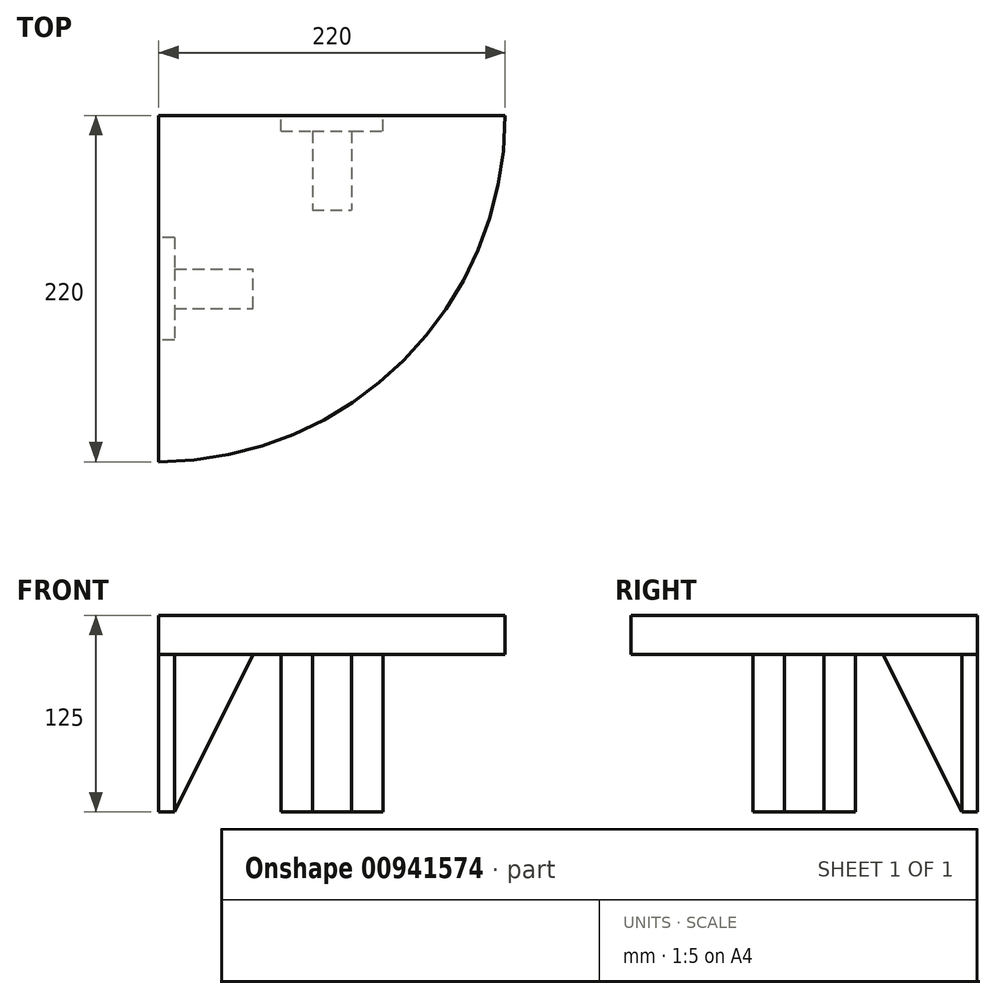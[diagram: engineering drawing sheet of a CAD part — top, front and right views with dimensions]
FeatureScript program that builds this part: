
annotation { "Feature Type Name" : "Feature", "Feature Type Description" : "" }
export const myFeature = defineFeature(function(context is Context, id is Id, definition is map)
    precondition{}
    {
        {
            var Q0;
            Q0=qCreatedBy(makeId("Top.planeOp"),FACE);
            var sketch = newSketch(context, id + "F0", { "sketchPlane" : qUnion([Q0])});
            skLineSegment(sketch, "E0", {"start": v(0, 0) * mm, "end": v(0, -220) * mm});
            skLineSegment(sketch, "E1", {"start": v(0, 0) * mm, "end": v(220, 0) * mm});
            skCircle(sketch, "E2", {"center": v(0, 0) * mm, "radius": 220 * mm});
            skSolve(sketch);
        }
        {
            var Q0;
            {var subQ0=sQuery(id+"F0.wireOp",EDGE,"E0");Q0=makeQuery(id+"F0.imprint","IMPRINT",FACE,{"disambiguationData":[TD([[makeQuery(id+"F0.imprint","IMPRINT",EDGE,{"derivedFrom":subQ0}),1.0]])]});}
            extrude(context, id + "F1", {"entities" : qUnion([Q0]), "oppositeDirection" : true, "depth" : 25 * mm, "offsetDistance" : 25 * mm});
        }
        {
            var Q0;
            Q0=makeQuery(id+"F1.opExtrude","SWEPT_FACE",FACE,{"disambiguationData":[OSD([sQuery(id+"F0.wireOp",EDGE,"E1")])]});
            var sketch = newSketch(context, id + "F2", { "sketchPlane" : qUnion([Q0])});
            skLineSegment(sketch, "E3", {"start": v(-110, -25) * mm, "end": v(-77.5, -25) * mm, "construction": true});
            skLineSegment(sketch, "E4.bottom", {"start": v(-77.5, -25) * mm, "end": v(-142.5, -25) * mm});
            skLineSegment(sketch, "E4.top", {"start": v(-77.5, -125) * mm, "end": v(-142.5, -125) * mm});
            skLineSegment(sketch, "E4.left", {"start": v(-77.5, -25) * mm, "end": v(-77.5, -125) * mm});
            skLineSegment(sketch, "E4.right", {"start": v(-142.5, -25) * mm, "end": v(-142.5, -125) * mm});
            skPoint(sketch, "E5", {"position": v(-122.5, -25) * mm});
            skLineSegment(sketch, "E6.bottom", {"start": v(-122.5, -25) * mm, "end": v(-97.5, -25) * mm});
            skLineSegment(sketch, "E6.top", {"start": v(-122.5, -125) * mm, "end": v(-97.5, -125) * mm});
            skLineSegment(sketch, "E6.left", {"start": v(-122.5, -25) * mm, "end": v(-122.5, -125) * mm});
            skLineSegment(sketch, "E6.right", {"start": v(-97.5, -25) * mm, "end": v(-97.5, -125) * mm});
            skSolve(sketch);
        }
        {
            var Q0;
            {var subQ0=sQuery(id+"F2.wireOp",EDGE,"E6.left");Q0=makeQuery(id+"F2.imprint","IMPRINT",FACE,{"disambiguationData":[TD([[makeQuery(id+"F2.imprint","IMPRINT",EDGE,{"derivedFrom":subQ0}),1.0]])]});}
            var Q1;
            {var subQ0=sQuery(id+"F2.wireOp",EDGE,"E4.right");Q1=makeQuery(id+"F2.imprint","IMPRINT",FACE,{"disambiguationData":[TD([[makeQuery(id+"F2.imprint","IMPRINT",EDGE,{"derivedFrom":subQ0}),1.0]])]});}
            var Q2;
            {var subQ0=sQuery(id+"F2.wireOp",EDGE,"E4.left");Q2=makeQuery(id+"F2.imprint","IMPRINT",FACE,{"disambiguationData":[TD([[makeQuery(id+"F2.imprint","IMPRINT",EDGE,{"derivedFrom":subQ0}),-1.0]])]});}
            extrude(context, id + "F3", {"entities" : qUnion([Q0, Q1, Q2]), "oppositeDirection" : true, "depth" : 10 * mm, "offsetDistance" : 25 * mm});
        }
        {
            var Q0;
            Q0=makeQuery(id+"F3.opExtrude","CAP_FACE",FACE,{"disambiguationData":[OSD([sQuery(id+"F2.wireOp",EDGE,"E4.bottom"),sQuery(id+"F2.wireOp",EDGE,"E4.top"),sQuery(id+"F2.wireOp",EDGE,"E4.left"),sQuery(id+"F2.wireOp",EDGE,"E4.right")])],"isStart":false});
            var sketch = newSketch(context, id + "F4", { "sketchPlane" : qUnion([Q0])});
            skLineSegment(sketch, "E7.bottom", {"start": v(97.5, -25) * mm, "end": v(122.5, -25) * mm});
            skLineSegment(sketch, "E7.top", {"start": v(97.5, -125) * mm, "end": v(122.5, -125) * mm});
            skLineSegment(sketch, "E7.left", {"start": v(97.5, -25) * mm, "end": v(97.5, -125) * mm});
            skLineSegment(sketch, "E7.right", {"start": v(122.5, -25) * mm, "end": v(122.5, -125) * mm});
            skSolve(sketch);
        }
        {
            var Q0;
            Q0=makeQuery(id+"F1.opExtrude","CAP_FACE",FACE,{"disambiguationData":[OSD([sQuery(id+"F0.wireOp",EDGE,"E0"),sQuery(id+"F0.wireOp",EDGE,"E1"),sQuery(id+"F0.wireOp",EDGE,"E2")])],"isStart":false});
            var sketch = newSketch(context, id + "F5", { "sketchPlane" : qUnion([Q0])});
            skLineSegment(sketch, "E8.bottom", {"start": v(97.5, 10) * mm, "end": v(122.5, 10) * mm});
            skLineSegment(sketch, "E8.top", {"start": v(97.5, 60) * mm, "end": v(122.5, 60) * mm});
            skLineSegment(sketch, "E8.left", {"start": v(97.5, 10) * mm, "end": v(97.5, 60) * mm});
            skLineSegment(sketch, "E8.right", {"start": v(122.5, 10) * mm, "end": v(122.5, 60) * mm});
            skSolve(sketch);
        }
        {
            var Q0;
            Q0=makeQuery(id+"F5.imprint","IMPRINT",FACE,{"disambiguationData":[TD([[makeQuery(id+"F5.imprint","IMPRINT",EDGE,{"derivedFrom":sQuery(id+"F5.wireOp",EDGE,"E8.bottom")}),-1.0]])]});
            var sketch = newSketch(context, id + "F6", { "sketchPlane" : qUnion([Q0])});
            skLineSegment(sketch, "E9.bottom", {"start": v(0, 122.5) * mm, "end": v(60, 122.5) * mm});
            skLineSegment(sketch, "E9.top", {"start": v(0, 97.5) * mm, "end": v(60, 97.5) * mm});
            skLineSegment(sketch, "E9.left", {"start": v(0, 122.5) * mm, "end": v(0, 97.5) * mm});
            skLineSegment(sketch, "E9.right", {"start": v(60, 122.5) * mm, "end": v(60, 97.5) * mm});
            skPoint(sketch, "E10", {"position": v(0, 122.5) * mm});
            skPoint(sketch, "E11", {"position": v(0, 110) * mm});
            skLineSegment(sketch, "E12", {"start": v(10, 122.5) * mm, "end": v(10, 97.5) * mm});
            skSolve(sketch);
        }
        {
            var Q0;
            Q0=makeQuery(id+"F1.opExtrude","SWEPT_FACE",FACE,{"disambiguationData":[OSD([sQuery(id+"F0.wireOp",EDGE,"E0")])]});
            var sketch = newSketch(context, id + "F7", { "sketchPlane" : qUnion([Q0])});
            skLineSegment(sketch, "E13.bottom", {"start": v(97.5, -25) * mm, "end": v(122.5, -25) * mm});
            skLineSegment(sketch, "E13.top", {"start": v(97.5, -125) * mm, "end": v(122.5, -125) * mm});
            skLineSegment(sketch, "E13.left", {"start": v(97.5, -25) * mm, "end": v(97.5, -125) * mm});
            skLineSegment(sketch, "E13.right", {"start": v(122.5, -25) * mm, "end": v(122.5, -125) * mm});
            skSolve(sketch);
        }
        {
            var Q0;
            Q0=makeQuery(id+"F7.imprint","IMPRINT",FACE,{"disambiguationData":[TD([[makeQuery(id+"F7.imprint","IMPRINT",EDGE,{"derivedFrom":sQuery(id+"F7.wireOp",EDGE,"E13.bottom")}),-1.0]])]});
            var sketch = newSketch(context, id + "F8", { "sketchPlane" : qUnion([Q0])});
            skLineSegment(sketch, "E14.bottom", {"start": v(77.5, -25) * mm, "end": v(142.5, -25) * mm});
            skLineSegment(sketch, "E14.top", {"start": v(77.5, -125) * mm, "end": v(142.5, -125) * mm});
            skLineSegment(sketch, "E14.left", {"start": v(77.5, -25) * mm, "end": v(77.5, -125) * mm});
            skLineSegment(sketch, "E14.right", {"start": v(142.5, -25) * mm, "end": v(142.5, -125) * mm});
            skPoint(sketch, "E15", {"position": v(110, -25) * mm});
            skSolve(sketch);
        }
        {
            var Q0;
            {var subQ1=makeQuery(id+"F7.imprint","IMPRINT",EDGE,{"derivedFrom":sQuery(id+"F7.wireOp",EDGE,"E13.left")});Q0=makeQuery(id+"F8.imprint","IMPRINT",FACE,{"disambiguationData":[TD([[makeQuery(id+"F8.imprint","IMPRINT",EDGE,{"derivedFrom":subQ1}),1.0]])]});}
            var Q1;
            {var subQ2=sQuery(id+"F8.wireOp",EDGE,"E14.left");Q1=makeQuery(id+"F8.imprint","IMPRINT",FACE,{"disambiguationData":[TD([[makeQuery(id+"F8.imprint","IMPRINT",EDGE,{"derivedFrom":subQ2}),1.0]])]});}
            var Q2;
            {var subQ2=sQuery(id+"F8.wireOp",EDGE,"E14.right");Q2=makeQuery(id+"F8.imprint","IMPRINT",FACE,{"disambiguationData":[TD([[makeQuery(id+"F8.imprint","IMPRINT",EDGE,{"derivedFrom":subQ2}),-1.0]])]});}
            extrude(context, id + "F9", {"entities" : qUnion([Q0, Q1, Q2]), "oppositeDirection" : true, "depth" : 10 * mm, "offsetDistance" : 25 * mm});
        }
        {
            var Q0;
            Q0=makeQuery(id+"F9.opExtrude","CAP_FACE",FACE,{"disambiguationData":[OSD([sQuery(id+"F8.wireOp",EDGE,"E14.bottom"),sQuery(id+"F8.wireOp",EDGE,"E14.top"),sQuery(id+"F8.wireOp",EDGE,"E14.left"),sQuery(id+"F8.wireOp",EDGE,"E14.right")])],"isStart":false});
            var sketch = newSketch(context, id + "F10", { "sketchPlane" : qUnion([Q0])});
            skLineSegment(sketch, "E16.bottom", {"start": v(-122.5, -125) * mm, "end": v(-97.5, -125) * mm});
            skLineSegment(sketch, "E16.top", {"start": v(-122.5, -25) * mm, "end": v(-97.5, -25) * mm});
            skLineSegment(sketch, "E16.left", {"start": v(-122.5, -125) * mm, "end": v(-122.5, -25) * mm});
            skLineSegment(sketch, "E16.right", {"start": v(-97.5, -125) * mm, "end": v(-97.5, -25) * mm});
            skSolve(sketch);
        }
        {
            var Q0;
            Q0=sQuery(id+"F5.wireOp",VERTEX,"E8.top.end");
            var Q1;
            Q1=makeQuery(id+"F3.opExtrude","SWEPT_FACE",FACE,{"disambiguationData":[OSD([sQuery(id+"F2.wireOp",EDGE,"E4.right")])]});
            cPlane(context, id + "F11", {"entities" : qUnion([Q0, Q1]), "cplaneType" : CPlaneType.PLANE_POINT, "offset" : 25 * mm, "width" : 150 * mm, "height" : 150 * mm});
        }
        {
            var Q0;
            Q0=qCreatedBy(id+"F11.planeOp",FACE);
            var sketch = newSketch(context, id + "F12", { "sketchPlane" : qUnion([Q0])});
            skLineSegment(sketch, "E17", {"start": v(-60, -25) * mm, "end": v(-10, -125) * mm});
            skSolve(sketch);
        }
        {
            var Q1;
            Q1=makeQuery(id+"F4.imprint","IMPRINT",FACE,{"disambiguationData":[TD([[makeQuery(id+"F4.imprint","IMPRINT",EDGE,{"derivedFrom":sQuery(id+"F4.wireOp",EDGE,"E7.bottom")}),-1.0]])]});
            var Q2;
            Q2=makeQuery(id+"F5.imprint","IMPRINT",FACE,{"disambiguationData":[TD([[makeQuery(id+"F5.imprint","IMPRINT",EDGE,{"derivedFrom":sQuery(id+"F5.wireOp",EDGE,"E8.bottom")}),1.0]])]});
            var Q3;
            Q3=sQuery(id+"F12.wireOp",EDGE,"E17");
            loft(context, id + "F13", {"operationType" : NewBodyOperationType.ADD, "addGuides" : true, "sheetProfilesArray" : [{ "sheetProfileEntities" : qUnion([Q1]) }, { "sheetProfileEntities" : qUnion([Q2]) }], "guidesArray" : [{ "guideEntities" : qUnion([Q3]), "guideDerivativeType" : LoftGuideDerivativeType.DEFAULT, "guideDerivativeMagnitude" : 1 }]});
        }
        {
            var Q0;
            Q0=sQuery(id+"F10.wireOp",VERTEX,"E16.left.end");
            var Q1;
            Q1=makeQuery(id+"F9.opExtrude","SWEPT_FACE",FACE,{"disambiguationData":[OSD([sQuery(id+"F8.wireOp",EDGE,"E14.right")])]});
            cPlane(context, id + "F14", {"entities" : qUnion([Q0, Q1]), "cplaneType" : CPlaneType.PLANE_POINT, "offset" : 25 * mm, "width" : 150 * mm, "height" : 150 * mm});
        }
        {
            var Q0;
            Q0=qCreatedBy(id+"F14.planeOp",FACE);
            var sketch = newSketch(context, id + "F15", { "sketchPlane" : qUnion([Q0])});
            skLineSegment(sketch, "E18", {"start": v(60, -25) * mm, "end": v(10, -125) * mm});
            skSolve(sketch);
        }
        {
            var Q1;
            {var subQ0=sQuery(id+"F6.wireOp",EDGE,"E9.right");Q1=makeQuery(id+"F6.imprint","IMPRINT",FACE,{"disambiguationData":[TD([[makeQuery(id+"F6.imprint","IMPRINT",EDGE,{"derivedFrom":subQ0}),-1.0]])]});}
            var Q2;
            Q2=makeQuery(id+"F10.imprint","IMPRINT",FACE,{"disambiguationData":[TD([[makeQuery(id+"F10.imprint","IMPRINT",EDGE,{"derivedFrom":sQuery(id+"F10.wireOp",EDGE,"E16.bottom")}),-1.0]])]});
            var Q3;
            Q3=sQuery(id+"F15.wireOp",EDGE,"E18");
            loft(context, id + "F16", {"operationType" : NewBodyOperationType.ADD, "addGuides" : true, "sheetProfilesArray" : [{ "sheetProfileEntities" : qUnion([Q1]) }, { "sheetProfileEntities" : qUnion([Q2]) }], "guidesArray" : [{ "guideEntities" : qUnion([Q3]), "guideDerivativeType" : LoftGuideDerivativeType.DEFAULT, "guideDerivativeMagnitude" : 1 }]});
        }
    });
